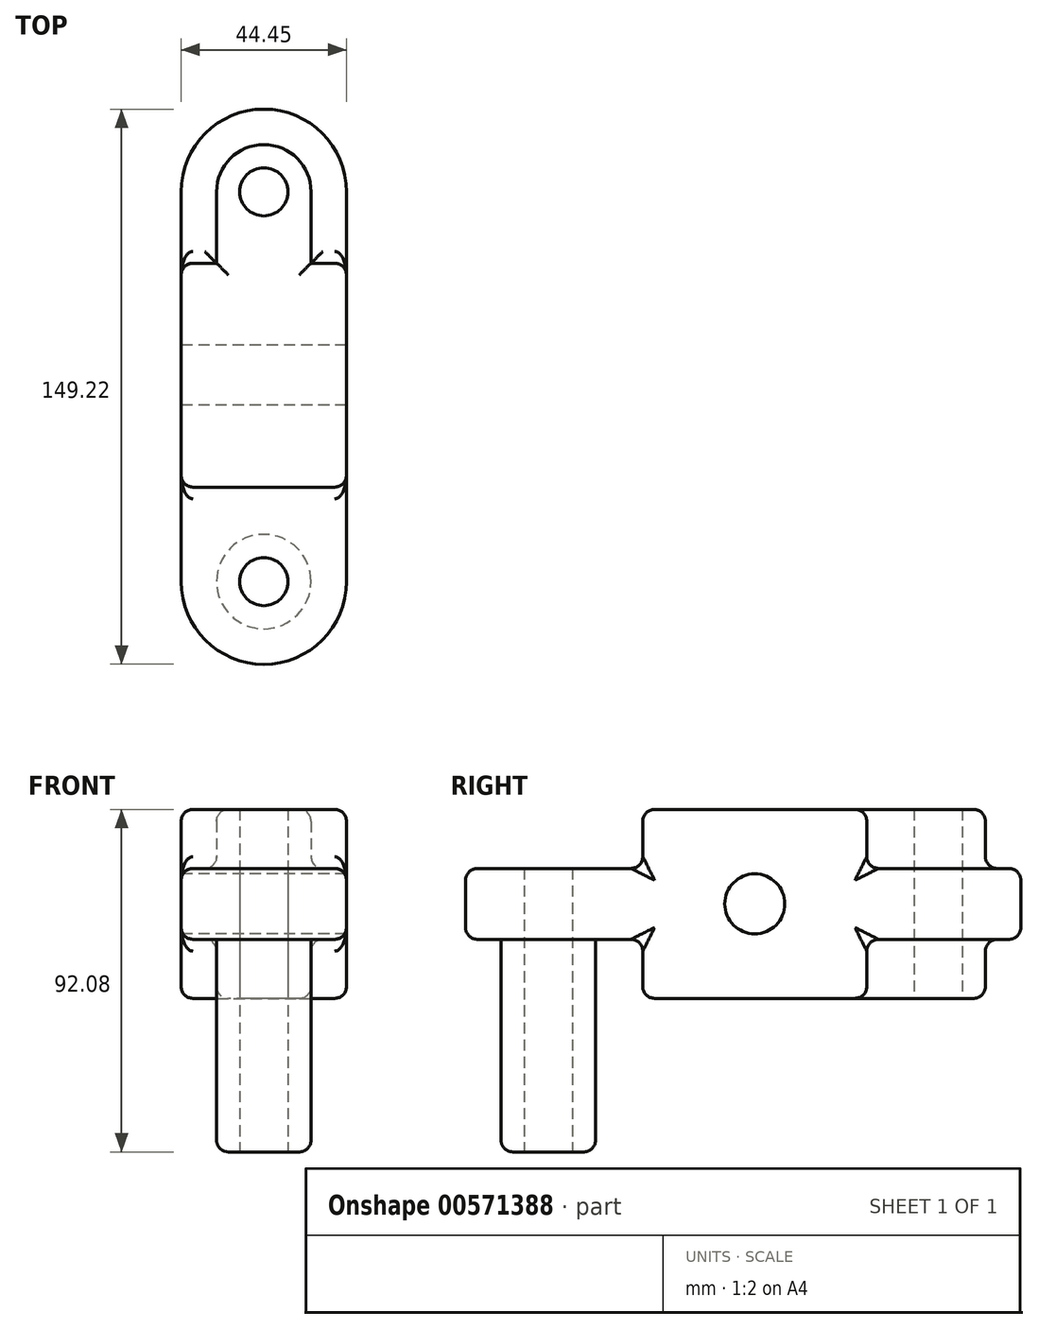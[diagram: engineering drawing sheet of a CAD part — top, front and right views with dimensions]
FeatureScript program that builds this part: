
annotation { "Feature Type Name" : "Feature", "Feature Type Description" : "" }
export const myFeature = defineFeature(function(context is Context, id is Id, definition is map)
    precondition{}
    {
        {
            var Q0;
            Q0=qCreatedBy(makeId("Top.planeOp"),FACE);
            var sketch = newSketch(context, id + "F0", { "sketchPlane" : qUnion([Q0])});
            skLineSegment(sketch, "E0.left", {"start": v(9.89, -20.4) * mm, "end": v(9.89, 84.37) * mm});
            skLineSegment(sketch, "E0.right", {"start": v(-34.56, -20.4) * mm, "end": v(-34.56, 84.37) * mm});
            skArc(sketch, "E1", {"start": v(9.89, 84.37) * mm, "mid": v(-12.34, 106.6) * mm, "end": v(-34.56, 84.37) * mm});
            skPoint(sketch, "E1.centerSnap0", {"position": v(-12.34, 106.6) * mm});
            skPoint(sketch, "E2.orphan", {"position": v(-34.56, 106.6) * mm});
            skPoint(sketch, "E3.orphan", {"position": v(9.89, 106.6) * mm});
            skCircle(sketch, "E4", {"center": v(-12.34, 84.37) * mm, "radius": 6.48 * mm});
            skArc(sketch, "E5", {"start": v(-34.56, -20.4) * mm, "mid": v(-12.34, -42.63) * mm, "end": v(9.89, -20.4) * mm});
            skCircle(sketch, "E6", {"center": v(-12.34, -20.4) * mm, "radius": 6.48 * mm});
            skCircle(sketch, "E7", {"center": v(-12.34, -20.4) * mm, "radius": 12.7 * mm});
            skLineSegment(sketch, "E8.bottom", {"start": v(-34.56, 65.19) * mm, "end": v(9.89, 65.19) * mm});
            skLineSegment(sketch, "E8.top", {"start": v(-34.56, 5) * mm, "end": v(9.89, 5) * mm});
            skLineSegment(sketch, "E8.left", {"start": v(-34.56, 65.19) * mm, "end": v(-34.56, 5) * mm});
            skArc(sketch, "E9", {"start": v(0.36, 84.37) * mm, "mid": v(-12.34, 97.07) * mm, "end": v(-25.04, 84.37) * mm});
            skLineSegment(sketch, "E10", {"start": v(0.36, 84.37) * mm, "end": v(0.36, 65.19) * mm});
            skLineSegment(sketch, "E11", {"start": v(-25.04, 84.37) * mm, "end": v(-25.04, 65.19) * mm});
            skSolve(sketch);
        }
        {
            var Q0;
            {var subQ5=sQuery(id+"F0.wireOp",EDGE,"E0.left");Q0=makeQuery(id+"F0.imprint","IMPRINT",FACE,{"disambiguationData":[TD([[makeQuery(id+"F0.imprint","IMPRINT",EDGE,{"derivedFrom":subQ5}),1.0]])]});}
            var Q1;
            Q1=makeQuery(id+"F0.imprint","IMPRINT",FACE,{"disambiguationData":[TD([[makeQuery(id+"F0.imprint","IMPRINT",EDGE,{"derivedFrom":sQuery(id+"F0.wireOp",EDGE,"E6")}),-1.0]])]});
            var Q2;
            Q2=makeQuery(id+"F0.imprint","IMPRINT",FACE,{"disambiguationData":[TD([[makeQuery(id+"F0.imprint","IMPRINT",EDGE,{"derivedFrom":sQuery(id+"F0.wireOp",EDGE,"E8.top")}),1.0]])]});
            var Q3;
            Q3=makeQuery(id+"F0.imprint","IMPRINT",FACE,{"disambiguationData":[TD([[makeQuery(id+"F0.imprint","IMPRINT",EDGE,{"derivedFrom":sQuery(id+"F0.wireOp",EDGE,"E4")}),-1.0]])]});
            var Q4;
            {var subQ4=sQuery(id+"F0.wireOp",EDGE,"E1");Q4=makeQuery(id+"F0.imprint","IMPRINT",FACE,{"disambiguationData":[TD([[makeQuery(id+"F0.imprint","IMPRINT",EDGE,{"derivedFrom":subQ4}),1.0]])]});}
            extrude(context, id + "F1", {"entities" : qUnion([Q0, Q1, Q2, Q3, Q4]), "depth" : 19.05 * mm, "offsetDistance" : 25.4 * mm});
        }
        {
            var Q0;
            Q0=makeQuery(id+"F0.imprint","IMPRINT",FACE,{"disambiguationData":[TD([[makeQuery(id+"F0.imprint","IMPRINT",EDGE,{"derivedFrom":sQuery(id+"F0.wireOp",EDGE,"E4")}),-1.0]])]});
            var Q1;
            Q1=makeQuery(id+"F0.imprint","IMPRINT",FACE,{"disambiguationData":[TD([[makeQuery(id+"F0.imprint","IMPRINT",EDGE,{"derivedFrom":sQuery(id+"F0.wireOp",EDGE,"E8.top")}),1.0]])]});
            extrude(context, id + "F2", {"entities" : qUnion([Q0, Q1]), "operationType" : NewBodyOperationType.ADD, "depth" : 34.92 * mm, "offsetDistance" : 25.4 * mm, "hasSecondDirection" : true, "secondDirectionOppositeDirection" : true, "secondDirectionDepth" : 15.88 * mm});
        }
        {
            var Q0;
            Q0=makeQuery(id+"F0.imprint","IMPRINT",FACE,{"disambiguationData":[TD([[makeQuery(id+"F0.imprint","IMPRINT",EDGE,{"derivedFrom":sQuery(id+"F0.wireOp",EDGE,"E6")}),-1.0]])]});
            extrude(context, id + "F3", {"entities" : qUnion([Q0]), "operationType" : NewBodyOperationType.ADD, "oppositeDirection" : true, "depth" : 57.15 * mm, "offsetDistance" : 25.4 * mm});
        }
        {
            var Q0;
            Q0=makeQuery(id+"F1.opExtrude","CAP_EDGE",EDGE,{"disambiguationData":[OSD([sQuery(id+"F0.wireOp",EDGE,"E5")])],"isStart":true});
            var Q1;
            Q1=makeQuery(id+"F1.opExtrude","CAP_EDGE",EDGE,{"disambiguationData":[OSD([sQuery(id+"F0.wireOp",EDGE,"E5")])],"isStart":false});
            var Q2;
            {var subQ0=sQuery(id+"F0.wireOp",EDGE,"E8.right");Q2=makeQuery(id+"F2.boolean.opBoolean","MERGE",FACE,{"derivedFrom":[makeQuery(id+"F1.opExtrude","SWEPT_FACE",FACE,{"disambiguationData":[OSD([sQuery(id+"F0.wireOp",EDGE,"E0.left"),subQ0])]}),makeQuery(id+"F2.opExtrude","SWEPT_FACE",FACE,{"disambiguationData":[OSD([subQ0])]})]});}
            var Q3;
            Q3=makeQuery(id+"F2.opExtrude","CAP_EDGE",EDGE,{"disambiguationData":[OSD([sQuery(id+"F0.wireOp",EDGE,"E11")])],"isStart":false});
            var Q4;
            Q4=makeQuery(id+"F2.opExtrude","CAP_EDGE",EDGE,{"disambiguationData":[OSD([sQuery(id+"F0.wireOp",EDGE,"E8.left")])],"isStart":false});
            var Q5;
            {var subQ0=sQuery(id+"F0.wireOp",EDGE,"E8.left");Q5=makeQuery(id+"F2.boolean.opBoolean","MERGE",FACE,{"derivedFrom":[makeQuery(id+"F1.opExtrude","SWEPT_FACE",FACE,{"disambiguationData":[OSD([sQuery(id+"F0.wireOp",EDGE,"E0.right"),subQ0])]}),makeQuery(id+"F2.opExtrude","SWEPT_FACE",FACE,{"disambiguationData":[OSD([subQ0])]})]});}
            var Q6;
            Q6=makeQuery(id+"F3.opExtrude","CAP_EDGE",EDGE,{"disambiguationData":[OSD([sQuery(id+"F0.wireOp",EDGE,"E7")])],"isStart":false});
            var Q7;
            Q7=makeQuery(id+"F2.opExtrude","CAP_EDGE",EDGE,{"disambiguationData":[OSD([sQuery(id+"F0.wireOp",EDGE,"E10")])],"isStart":true});
            var Q8;
            {var subQ0=sQuery(id+"F0.wireOp",EDGE,"E8.bottom");Q8=makeQuery(id+"F2.opExtrude","CAP_EDGE",EDGE,{"disambiguationData":[OSD([subQ0]),TDD([makeQuery(id+"F0.imprint","IMPRINT",EDGE,{"disambiguationData":[TD([[makeQuery(id+"F0.imprint","INTERSECT",VERTEX,{"derivedFrom":[subQ0,sQuery(id+"F0.wireOp",EDGE,"E11")]}),1.0]])],"derivedFrom":subQ0})])],"isStart":true});}
            var Q9;
            {var subQ0=sQuery(id+"F0.wireOp",EDGE,"E8.bottom");Q9=makeQuery(id+"F2.opExtrude","CAP_EDGE",EDGE,{"disambiguationData":[OSD([subQ0]),TDD([makeQuery(id+"F0.imprint","IMPRINT",EDGE,{"disambiguationData":[TD([[makeQuery(id+"F0.imprint","INTERSECT",VERTEX,{"derivedFrom":[subQ0,sQuery(id+"F0.wireOp",EDGE,"E10")]}),-1.0]])],"derivedFrom":subQ0})])],"isStart":true});}
            var Q10;
            Q10=makeQuery(id+"F2.opExtrude","CAP_EDGE",EDGE,{"disambiguationData":[OSD([sQuery(id+"F0.wireOp",EDGE,"E8.top")])],"isStart":true});
            var Q11;
            Q11=makeQuery(id+"F2.opExtrude","CAP_EDGE",EDGE,{"disambiguationData":[OSD([sQuery(id+"F0.wireOp",EDGE,"E8.top")])],"isStart":false});
            var Q12;
            {var subQ0=sQuery(id+"F0.wireOp",EDGE,"E8.bottom");Q12=makeQuery(id+"F2.opExtrude","CAP_EDGE",EDGE,{"disambiguationData":[OSD([subQ0]),TDD([makeQuery(id+"F0.imprint","IMPRINT",EDGE,{"disambiguationData":[TD([[makeQuery(id+"F0.imprint","INTERSECT",VERTEX,{"derivedFrom":[subQ0,sQuery(id+"F0.wireOp",EDGE,"E11")]}),1.0]])],"derivedFrom":subQ0})])],"isStart":false});}
            var Q13;
            {var subQ0=sQuery(id+"F0.wireOp",EDGE,"E8.bottom");Q13=makeQuery(id+"F2.opExtrude","CAP_EDGE",EDGE,{"disambiguationData":[OSD([subQ0]),TDD([makeQuery(id+"F0.imprint","IMPRINT",EDGE,{"disambiguationData":[TD([[makeQuery(id+"F0.imprint","INTERSECT",VERTEX,{"derivedFrom":[subQ0,sQuery(id+"F0.wireOp",EDGE,"E10")]}),-1.0]])],"derivedFrom":subQ0})])],"isStart":false});}
            fillet(context, id + "F4", {"entities" : qUnion([Q0, Q1, Q2, Q3, Q4, Q5, Q6, Q7, Q8, Q9, Q10, Q11, Q12, Q13]), "radius" : 3.17 * mm, "tangentPropagation" : true, "allowEdgeOverflow" : false});
        }
        {
            var Q0;
            {var subQ0=sQuery(id+"F0.wireOp",EDGE,"E8.left");Q0=makeQuery(id+"F2.boolean.opBoolean","MERGE",FACE,{"derivedFrom":[makeQuery(id+"F1.opExtrude","SWEPT_FACE",FACE,{"disambiguationData":[OSD([sQuery(id+"F0.wireOp",EDGE,"E0.right"),subQ0])]}),makeQuery(id+"F2.opExtrude","SWEPT_FACE",FACE,{"disambiguationData":[OSD([subQ0])]})]});}
            var sketch = newSketch(context, id + "F5", { "sketchPlane" : qUnion([Q0])});
            skCircle(sketch, "E12", {"center": v(-35.1, 9.53) * mm, "radius": 8.06 * mm});
            skPoint(sketch, "E12.centerSnap0", {"position": v(20.4, 9.53) * mm});
            skPoint(sketch, "E12.centerSnap1", {"position": v(-35.1, -12.7) * mm});
            skSolve(sketch);
        }
        {
            var Q0;
            Q0=makeQuery(id+"F5.imprint","IMPRINT",FACE,{"disambiguationData":[TD([[makeQuery(id+"F5.imprint","IMPRINT",EDGE,{"derivedFrom":sQuery(id+"F5.wireOp",EDGE,"E12")}),1.0]])]});
            extrude(context, id + "F6", {"entities" : qUnion([Q0]), "operationType" : NewBodyOperationType.REMOVE, "endBound" : BoundingType.THROUGH_ALL, "oppositeDirection" : true, "depth" : 25.4 * mm, "offsetDistance" : 25.4 * mm});
        }
        {
            var Q0;
            Q0=makeQuery(id+"F2.boolean.opBoolean","INTERSECT",EDGE,{"derivedFrom":[makeQuery(id+"F1.opExtrude","CAP_FACE",FACE,{"disambiguationData":[OSD([sQuery(id+"F0.wireOp",EDGE,"E0.left"),sQuery(id+"F0.wireOp",EDGE,"E0.right"),sQuery(id+"F0.wireOp",EDGE,"E1"),sQuery(id+"F0.wireOp",EDGE,"E4"),sQuery(id+"F0.wireOp",EDGE,"E5"),sQuery(id+"F0.wireOp",EDGE,"E6"),sQuery(id+"F0.wireOp",EDGE,"E8.left"),sQuery(id+"F0.wireOp",EDGE,"E8.right")])],"isStart":false}),makeQuery(id+"F2.opExtrude","SWEPT_FACE",FACE,{"disambiguationData":[OSD([sQuery(id+"F0.wireOp",EDGE,"E8.top")])]})]});
            var Q1;
            Q1=makeQuery(id+"F3.opExtrude","CAP_EDGE",EDGE,{"disambiguationData":[OSD([sQuery(id+"F0.wireOp",EDGE,"E7")])],"isStart":true});
            var Q2;
            Q2=makeQuery(id+"F2.boolean.opBoolean","INTERSECT",EDGE,{"derivedFrom":[makeQuery(id+"F1.opExtrude","CAP_FACE",FACE,{"disambiguationData":[OSD([sQuery(id+"F0.wireOp",EDGE,"E0.left"),sQuery(id+"F0.wireOp",EDGE,"E0.right"),sQuery(id+"F0.wireOp",EDGE,"E1"),sQuery(id+"F0.wireOp",EDGE,"E4"),sQuery(id+"F0.wireOp",EDGE,"E5"),sQuery(id+"F0.wireOp",EDGE,"E6"),sQuery(id+"F0.wireOp",EDGE,"E8.left"),sQuery(id+"F0.wireOp",EDGE,"E8.right")])],"isStart":true}),makeQuery(id+"F2.opExtrude","SWEPT_FACE",FACE,{"disambiguationData":[OSD([sQuery(id+"F0.wireOp",EDGE,"E8.top")])]})]});
            var Q3;
            Q3=makeQuery(id+"F2.boolean.opBoolean","INTERSECT",EDGE,{"derivedFrom":[makeQuery(id+"F1.opExtrude","CAP_FACE",FACE,{"disambiguationData":[OSD([sQuery(id+"F0.wireOp",EDGE,"E0.left"),sQuery(id+"F0.wireOp",EDGE,"E0.right"),sQuery(id+"F0.wireOp",EDGE,"E1"),sQuery(id+"F0.wireOp",EDGE,"E4"),sQuery(id+"F0.wireOp",EDGE,"E5"),sQuery(id+"F0.wireOp",EDGE,"E6"),sQuery(id+"F0.wireOp",EDGE,"E8.left"),sQuery(id+"F0.wireOp",EDGE,"E8.right")])],"isStart":true}),makeQuery(id+"F2.opExtrude","SWEPT_FACE",FACE,{"disambiguationData":[OSD([sQuery(id+"F0.wireOp",EDGE,"E11")])]})]});
            var Q4;
            Q4=makeQuery(id+"F2.boolean.opBoolean","INTERSECT",EDGE,{"derivedFrom":[makeQuery(id+"F1.opExtrude","CAP_FACE",FACE,{"disambiguationData":[OSD([sQuery(id+"F0.wireOp",EDGE,"E0.left"),sQuery(id+"F0.wireOp",EDGE,"E0.right"),sQuery(id+"F0.wireOp",EDGE,"E1"),sQuery(id+"F0.wireOp",EDGE,"E4"),sQuery(id+"F0.wireOp",EDGE,"E5"),sQuery(id+"F0.wireOp",EDGE,"E6"),sQuery(id+"F0.wireOp",EDGE,"E8.left"),sQuery(id+"F0.wireOp",EDGE,"E8.right")])],"isStart":false}),makeQuery(id+"F2.opExtrude","SWEPT_FACE",FACE,{"disambiguationData":[OSD([sQuery(id+"F0.wireOp",EDGE,"E10")])]})]});
            var Q5;
            {var subQ0=sQuery(id+"F0.wireOp",EDGE,"E8.right");var subQ1=sQuery(id+"F0.wireOp",EDGE,"E8.bottom");var subQ2=sQuery(id+"F0.wireOp",EDGE,"E0.left");Q5=makeQuery(id+"F2.boolean.opBoolean","INTERSECT",EDGE,{"derivedFrom":[makeQuery(id+"F1.opExtrude","CAP_FACE",FACE,{"disambiguationData":[OSD([subQ2,sQuery(id+"F0.wireOp",EDGE,"E0.right"),sQuery(id+"F0.wireOp",EDGE,"E1"),sQuery(id+"F0.wireOp",EDGE,"E4"),sQuery(id+"F0.wireOp",EDGE,"E5"),sQuery(id+"F0.wireOp",EDGE,"E6"),sQuery(id+"F0.wireOp",EDGE,"E8.left"),subQ0])],"isStart":false}),makeQuery(id+"F2.opExtrude","SWEPT_FACE",FACE,{"disambiguationData":[OSD([subQ1]),TDD([makeQuery(id+"F0.imprint","IMPRINT",EDGE,{"disambiguationData":[TD([[makeQuery(id+"F0.imprint","INTERSECT",VERTEX,{"derivedFrom":[subQ1,sQuery(id+"F0.wireOp",EDGE,"E10")]}),-1.0]])],"derivedFrom":subQ1})])]})]});}
            var Q6;
            {var subQ0=sQuery(id+"F0.wireOp",EDGE,"E8.left");var subQ1=sQuery(id+"F0.wireOp",EDGE,"E8.bottom");var subQ2=sQuery(id+"F0.wireOp",EDGE,"E0.right");Q6=makeQuery(id+"F2.boolean.opBoolean","INTERSECT",EDGE,{"derivedFrom":[makeQuery(id+"F1.opExtrude","CAP_FACE",FACE,{"disambiguationData":[OSD([sQuery(id+"F0.wireOp",EDGE,"E0.left"),subQ2,sQuery(id+"F0.wireOp",EDGE,"E1"),sQuery(id+"F0.wireOp",EDGE,"E4"),sQuery(id+"F0.wireOp",EDGE,"E5"),sQuery(id+"F0.wireOp",EDGE,"E6"),subQ0,sQuery(id+"F0.wireOp",EDGE,"E8.right")])],"isStart":false}),makeQuery(id+"F2.opExtrude","SWEPT_FACE",FACE,{"disambiguationData":[OSD([subQ1]),TDD([makeQuery(id+"F0.imprint","IMPRINT",EDGE,{"disambiguationData":[TD([[makeQuery(id+"F0.imprint","INTERSECT",VERTEX,{"derivedFrom":[subQ1,sQuery(id+"F0.wireOp",EDGE,"E11")]}),1.0]])],"derivedFrom":subQ1})])]})]});}
            var Q7;
            {var subQ0=sQuery(id+"F0.wireOp",EDGE,"E8.left");var subQ1=sQuery(id+"F0.wireOp",EDGE,"E8.bottom");var subQ2=sQuery(id+"F0.wireOp",EDGE,"E0.right");Q7=makeQuery(id+"F2.boolean.opBoolean","INTERSECT",EDGE,{"derivedFrom":[makeQuery(id+"F1.opExtrude","CAP_FACE",FACE,{"disambiguationData":[OSD([sQuery(id+"F0.wireOp",EDGE,"E0.left"),subQ2,sQuery(id+"F0.wireOp",EDGE,"E1"),sQuery(id+"F0.wireOp",EDGE,"E4"),sQuery(id+"F0.wireOp",EDGE,"E5"),sQuery(id+"F0.wireOp",EDGE,"E6"),subQ0,sQuery(id+"F0.wireOp",EDGE,"E8.right")])],"isStart":true}),makeQuery(id+"F2.opExtrude","SWEPT_FACE",FACE,{"disambiguationData":[OSD([subQ1]),TDD([makeQuery(id+"F0.imprint","IMPRINT",EDGE,{"disambiguationData":[TD([[makeQuery(id+"F0.imprint","INTERSECT",VERTEX,{"derivedFrom":[subQ1,sQuery(id+"F0.wireOp",EDGE,"E11")]}),1.0]])],"derivedFrom":subQ1})])]})]});}
            var Q8;
            {var subQ0=sQuery(id+"F0.wireOp",EDGE,"E8.right");var subQ1=sQuery(id+"F0.wireOp",EDGE,"E8.bottom");var subQ2=sQuery(id+"F0.wireOp",EDGE,"E0.left");Q8=makeQuery(id+"F2.boolean.opBoolean","INTERSECT",EDGE,{"derivedFrom":[makeQuery(id+"F1.opExtrude","CAP_FACE",FACE,{"disambiguationData":[OSD([subQ2,sQuery(id+"F0.wireOp",EDGE,"E0.right"),sQuery(id+"F0.wireOp",EDGE,"E1"),sQuery(id+"F0.wireOp",EDGE,"E4"),sQuery(id+"F0.wireOp",EDGE,"E5"),sQuery(id+"F0.wireOp",EDGE,"E6"),sQuery(id+"F0.wireOp",EDGE,"E8.left"),subQ0])],"isStart":true}),makeQuery(id+"F2.opExtrude","SWEPT_FACE",FACE,{"disambiguationData":[OSD([subQ1]),TDD([makeQuery(id+"F0.imprint","IMPRINT",EDGE,{"disambiguationData":[TD([[makeQuery(id+"F0.imprint","INTERSECT",VERTEX,{"derivedFrom":[subQ1,sQuery(id+"F0.wireOp",EDGE,"E10")]}),-1.0]])],"derivedFrom":subQ1})])]})]});}
            fillet(context, id + "F7", {"entities" : qUnion([Q0, Q1, Q2, Q3, Q4, Q5, Q6, Q7, Q8]), "radius" : 3.17 * mm, "tangentPropagation" : true, "allowEdgeOverflow" : false});
        }
    });
